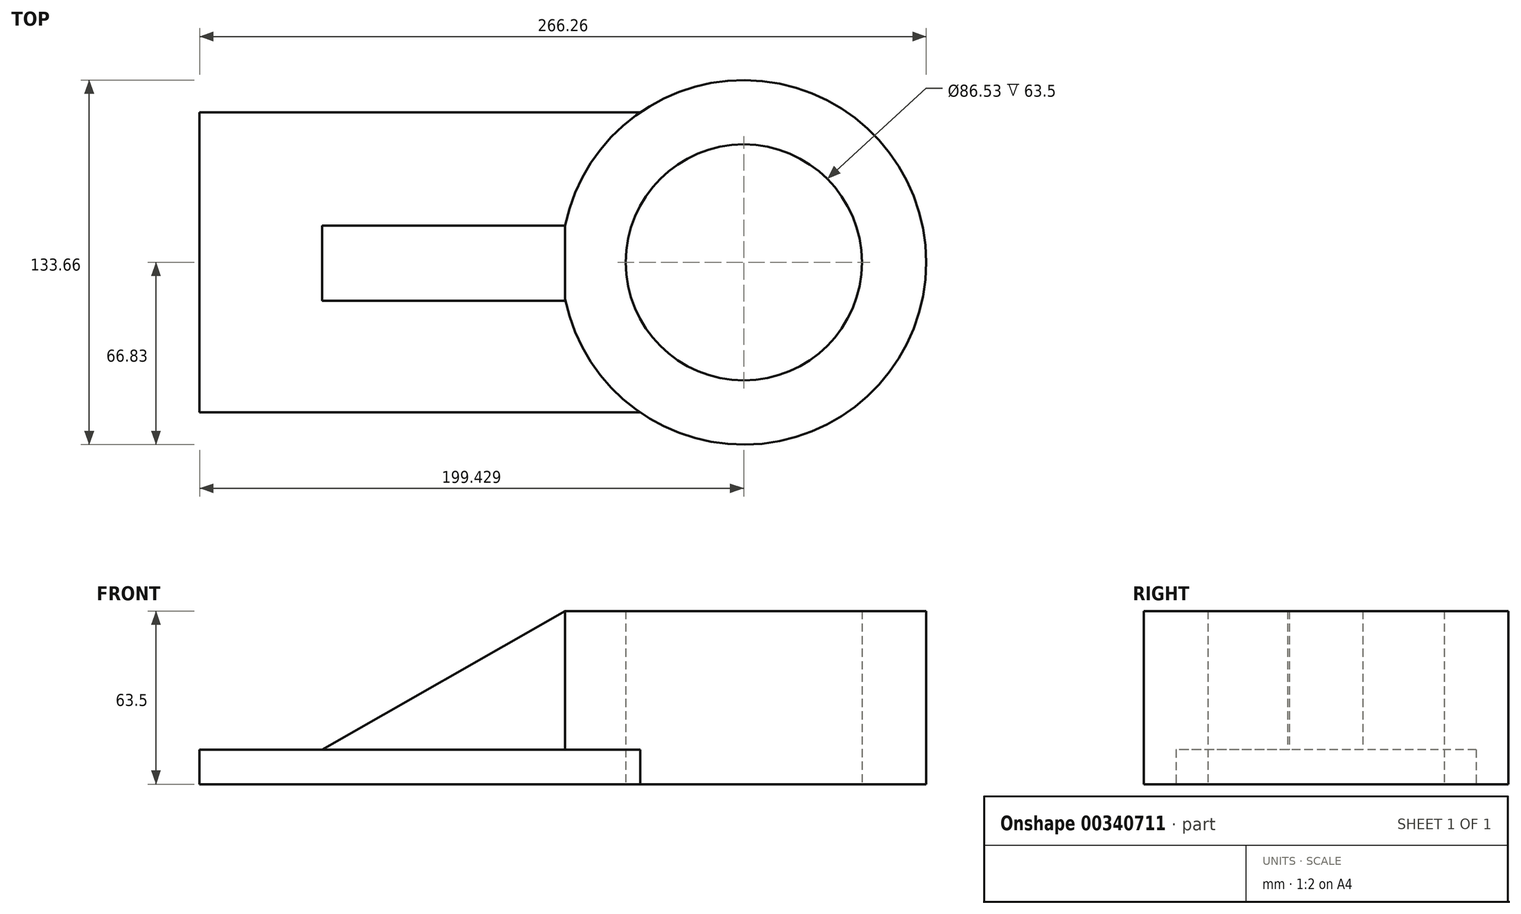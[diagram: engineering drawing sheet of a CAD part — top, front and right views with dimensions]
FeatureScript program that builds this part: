
annotation { "Feature Type Name" : "Feature", "Feature Type Description" : "" }
export const myFeature = defineFeature(function(context is Context, id is Id, definition is map)
    precondition{}
    {
        {
            var Q0;
            Q0=qCreatedBy(makeId("Top.planeOp"),FACE);
            var sketch = newSketch(context, id + "F0", { "sketchPlane" : qUnion([Q0])});
            skCircle(sketch, "E0", {"center": v(85.97, 0) * mm, "radius": 66.83 * mm});
            skLineSegment(sketch, "E1.bottom", {"start": v(47.97, 54.98) * mm, "end": v(-113.46, 54.98) * mm});
            skLineSegment(sketch, "E1.top", {"start": v(47.97, -54.98) * mm, "end": v(-113.46, -54.98) * mm});
            skLineSegment(sketch, "E1.right", {"start": v(-113.46, 54.98) * mm, "end": v(-113.46, -54.98) * mm});
            skCircle(sketch, "E2", {"center": v(85.97, 0) * mm, "radius": 43.27 * mm});
            skSolve(sketch);
        }
        {
            var Q0;
            Q0=makeQuery(id+"F0.imprint","IMPRINT",FACE,{"disambiguationData":[TD([[makeQuery(id+"F0.imprint","IMPRINT",EDGE,{"derivedFrom":sQuery(id+"F0.wireOp",EDGE,"E2")}),-1.0]])]});
            var Q1;
            {var subQ0=sQuery(id+"F0.wireOp",EDGE,"E1.bottom");Q1=makeQuery(id+"F0.imprint","IMPRINT",FACE,{"disambiguationData":[TD([[makeQuery(id+"F0.imprint","IMPRINT",EDGE,{"derivedFrom":subQ0}),1.0]])]});}
            extrude(context, id + "F1", {"entities" : qUnion([Q0, Q1]), "depth" : 12.7 * mm});
        }
        {
            var Q0;
            Q0=makeQuery(id+"F0.imprint","IMPRINT",FACE,{"disambiguationData":[TD([[makeQuery(id+"F0.imprint","IMPRINT",EDGE,{"derivedFrom":sQuery(id+"F0.wireOp",EDGE,"E2")}),-1.0]])]});
            extrude(context, id + "F2", {"entities" : qUnion([Q0]), "operationType" : NewBodyOperationType.ADD, "depth" : 63.5 * mm});
        }
        {
            var Q0;
            Q0=makeQuery(id+"F1.opExtrude","CAP_FACE",FACE,{"disambiguationData":[OSD([sQuery(id+"F0.wireOp",EDGE,"E0"),sQuery(id+"F0.wireOp",EDGE,"E1.bottom"),sQuery(id+"F0.wireOp",EDGE,"E1.top"),sQuery(id+"F0.wireOp",EDGE,"E1.right"),sQuery(id+"F0.wireOp",EDGE,"E2")])],"isStart":false});
            var sketch = newSketch(context, id + "F3", { "sketchPlane" : qUnion([Q0])});
            skLineSegment(sketch, "E3.bottom", {"start": v(20.5, 13.46) * mm, "end": v(-68.55, 13.46) * mm});
            skLineSegment(sketch, "E3.top", {"start": v(20.5, -14.13) * mm, "end": v(-68.55, -14.13) * mm});
            skLineSegment(sketch, "E3.left", {"start": v(20.5, 13.46) * mm, "end": v(20.5, -14.13) * mm});
            skLineSegment(sketch, "E3.right", {"start": v(-68.55, 13.46) * mm, "end": v(-68.55, -14.13) * mm});
            skSolve(sketch);
        }
        {
            var Q0;
            {var subQ5=sQuery(id+"F3.wireOp",EDGE,"E3.bottom");Q0=makeQuery(id+"F3.imprint","IMPRINT",FACE,{"disambiguationData":[TD([[makeQuery(id+"F3.imprint","IMPRINT",EDGE,{"derivedFrom":subQ5}),1.0]])]});}
            extrude(context, id + "F4", {"entities" : qUnion([Q0]), "operationType" : NewBodyOperationType.ADD, "depth" : 50.8 * mm});
        }
        {
            var Q0;
            Q0=makeQuery(id+"F4.opExtrude","SWEPT_FACE",FACE,{"disambiguationData":[OSD([sQuery(id+"F3.wireOp",EDGE,"E3.top")])]});
            var sketch = newSketch(context, id + "F5", { "sketchPlane" : qUnion([Q0])});
            skLineSegment(sketch, "E4", {"start": v(20.5, 63.5) * mm, "end": v(-68.55, 12.7) * mm});
            skLineSegment(sketch, "E5", {"start": v(-68.55, 12.7) * mm, "end": v(-68.55, 63.5) * mm});
            skLineSegment(sketch, "E6", {"start": v(-68.55, 63.5) * mm, "end": v(20.5, 63.5) * mm});
            skSolve(sketch);
        }
        {
            var Q0;
            Q0=makeQuery(id+"F5.imprint","IMPRINT",FACE,{"disambiguationData":[TD([[makeQuery(id+"F5.imprint","IMPRINT",EDGE,{"derivedFrom":sQuery(id+"F5.wireOp",EDGE,"E4")}),-1.0]])]});
            var Q1;
            Q1=makeQuery(id+"F4.opExtrude","SWEPT_FACE",FACE,{"disambiguationData":[OSD([sQuery(id+"F3.wireOp",EDGE,"E3.bottom")])]});
            extrude(context, id + "F6", {"entities" : qUnion([Q0]), "operationType" : NewBodyOperationType.REMOVE, "endBound" : BoundingType.THROUGH_ALL, "oppositeDirection" : true, "endBoundEntityFace" : qUnion([Q1]), "depth" : 25.4 * mm});
        }
    });
